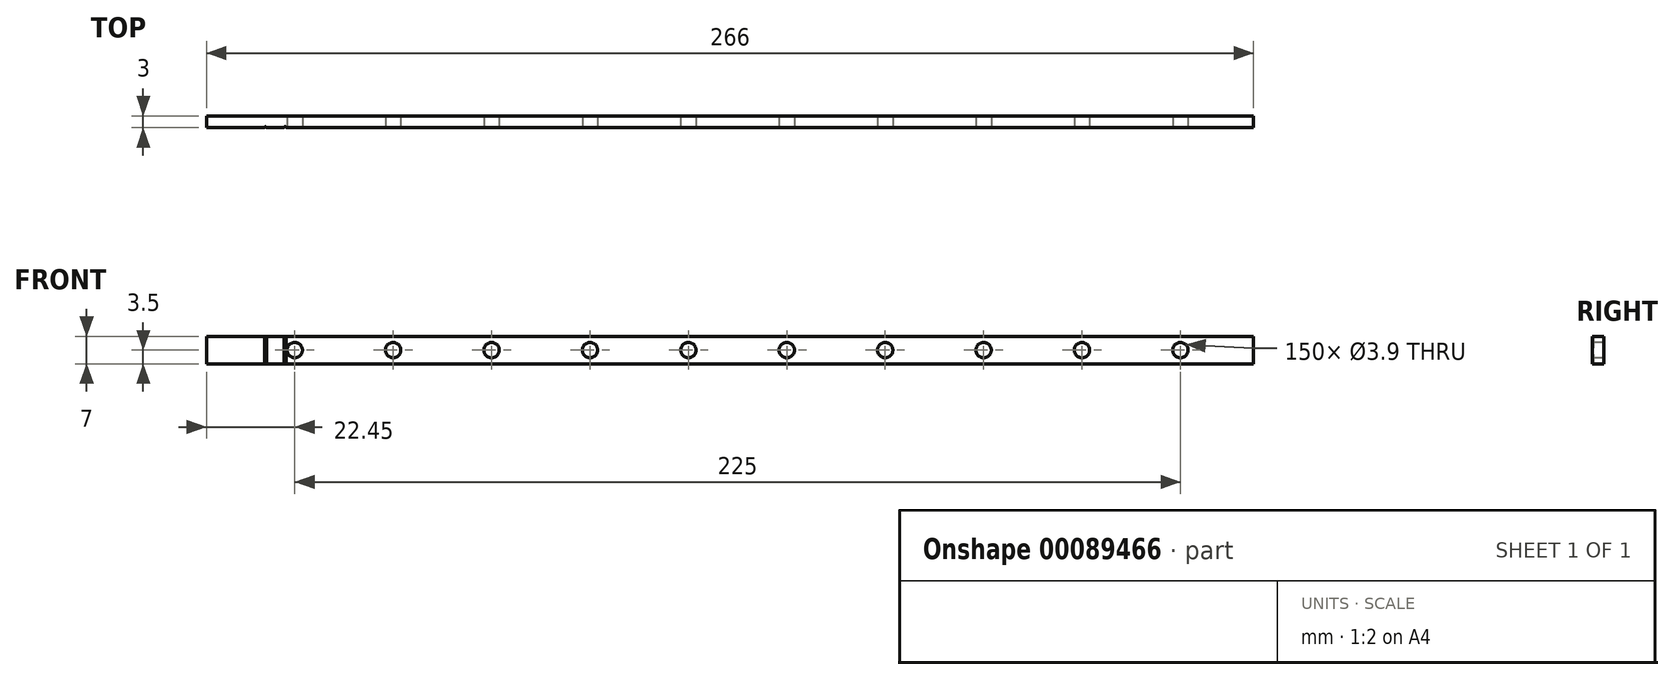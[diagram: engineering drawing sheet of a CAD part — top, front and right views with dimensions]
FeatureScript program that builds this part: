
annotation { "Feature Type Name" : "Feature", "Feature Type Description" : "" }
export const myFeature = defineFeature(function(context is Context, id is Id, definition is map)
    precondition{}
    {
        {
            var Q0;
            Q0=qCreatedBy(makeId("Front.planeOp"),FACE);
            var sketch = newSketch(context, id + "F0", { "sketchPlane" : qUnion([Q0])});
            skLineSegment(sketch, "E0.bottom", {"start": v(-1767.63, 127) * mm, "end": v(1767.63, 127) * mm});
            skLineSegment(sketch, "E0.top", {"start": v(-1767.63, -127) * mm, "end": v(1767.63, -127) * mm});
            skLineSegment(sketch, "E0.left", {"start": v(-1767.63, 127) * mm, "end": v(-1767.63, -127) * mm});
            skLineSegment(sketch, "E0.right", {"start": v(1767.63, 127) * mm, "end": v(1767.63, -127) * mm});
            skPoint(sketch, "E0.middle", {"position": v(0, 0) * mm});
            skLineSegment(sketch, "E1.bottom", {"start": v(-133, 3.5) * mm, "end": v(133, 3.5) * mm});
            skLineSegment(sketch, "E1.top", {"start": v(-133, -3.5) * mm, "end": v(133, -3.5) * mm});
            skLineSegment(sketch, "E1.left", {"start": v(-133, 3.5) * mm, "end": v(-133, -3.5) * mm});
            skLineSegment(sketch, "E1.right", {"start": v(133, 3.5) * mm, "end": v(133, -3.5) * mm});
            skSolve(sketch);
        }
        {
            var Q0;
            Q0=makeQuery(id+"F0.imprint","IMPRINT",FACE,{"disambiguationData":[TD([[makeQuery(id+"F0.imprint","IMPRINT",EDGE,{"derivedFrom":sQuery(id+"F0.wireOp",EDGE,"E1.bottom")}),-1.0]])]});
            extrude(context, id + "F1", {"entities" : qUnion([Q0]), "depth" : 3 * mm});
        }
        {
            var Q0;
            Q0=makeQuery(id+"F1.opExtrude","CAP_FACE",FACE,{"disambiguationData":[OSD([sQuery(id+"F0.wireOp",EDGE,"E1.bottom"),sQuery(id+"F0.wireOp",EDGE,"E1.top"),sQuery(id+"F0.wireOp",EDGE,"E1.left"),sQuery(id+"F0.wireOp",EDGE,"E1.right")])],"isStart":false});
            var sketch = newSketch(context, id + "F2", { "sketchPlane" : qUnion([Q0])});
            skCircle(sketch, "E2", {"center": v(-110.55, 0) * mm, "radius": 1.95 * mm});
            skCircle(sketch, "E3.1.0.0", {"center": v(-85.55, 0) * mm, "radius": 1.95 * mm});
            skCircle(sketch, "E3.2.0.0", {"center": v(-60.55, 0) * mm, "radius": 1.95 * mm});
            skCircle(sketch, "E3.3.0.0", {"center": v(-35.55, 0) * mm, "radius": 1.95 * mm});
            skCircle(sketch, "E3.4.0.0", {"center": v(-10.55, 0) * mm, "radius": 1.95 * mm});
            skCircle(sketch, "E3.5.0.0", {"center": v(14.45, 0) * mm, "radius": 1.95 * mm});
            skCircle(sketch, "E3.6.0.0", {"center": v(39.45, 0) * mm, "radius": 1.95 * mm});
            skCircle(sketch, "E3.7.0.0", {"center": v(64.45, 0) * mm, "radius": 1.95 * mm});
            skCircle(sketch, "E3.8.0.0", {"center": v(89.45, 0) * mm, "radius": 1.95 * mm});
            skCircle(sketch, "E3.9.0.0", {"center": v(114.45, 0) * mm, "radius": 1.95 * mm});
            skLineSegment(sketch, "E3.direction1", {"start": v(-110.55, 0) * mm, "end": v(-85.55, 0) * mm, "construction": true});
            skSolve(sketch);
        }
        {
            var Q0;
            Q0 = qSketchRegion(id + "F2", true);
            extrude(context, id + "F3", {"entities" : qUnion([Q0]), "operationType" : NewBodyOperationType.REMOVE, "endBound" : BoundingType.THROUGH_ALL, "oppositeDirection" : true, "depth" : 25 * mm});
        }
        {
            var Q0;
            Q0=makeQuery(id+"F1.opExtrude","SWEPT_FACE",FACE,{"disambiguationData":[OSD([sQuery(id+"F0.wireOp",EDGE,"E1.top")])]});
            var sketch = newSketch(context, id + "F4", { "sketchPlane" : qUnion([Q0])});
            skCircle(sketch, "E4", {"center": v(-118, 3) * mm, "radius": 0.25 * mm});
            skCircle(sketch, "E5.1.0.0", {"center": v(-113, 3) * mm, "radius": 0.25 * mm});
            skLineSegment(sketch, "E5.direction1", {"start": v(-118, 3) * mm, "end": v(-113, 3) * mm, "construction": true});
            skSolve(sketch);
        }
        {
            var Q0;
            Q0 = qSketchRegion(id + "F4", true);
            extrude(context, id + "F5", {"entities" : qUnion([Q0]), "operationType" : NewBodyOperationType.REMOVE, "endBound" : BoundingType.THROUGH_ALL, "oppositeDirection" : true, "depth" : 25 * mm});
        }
    });
